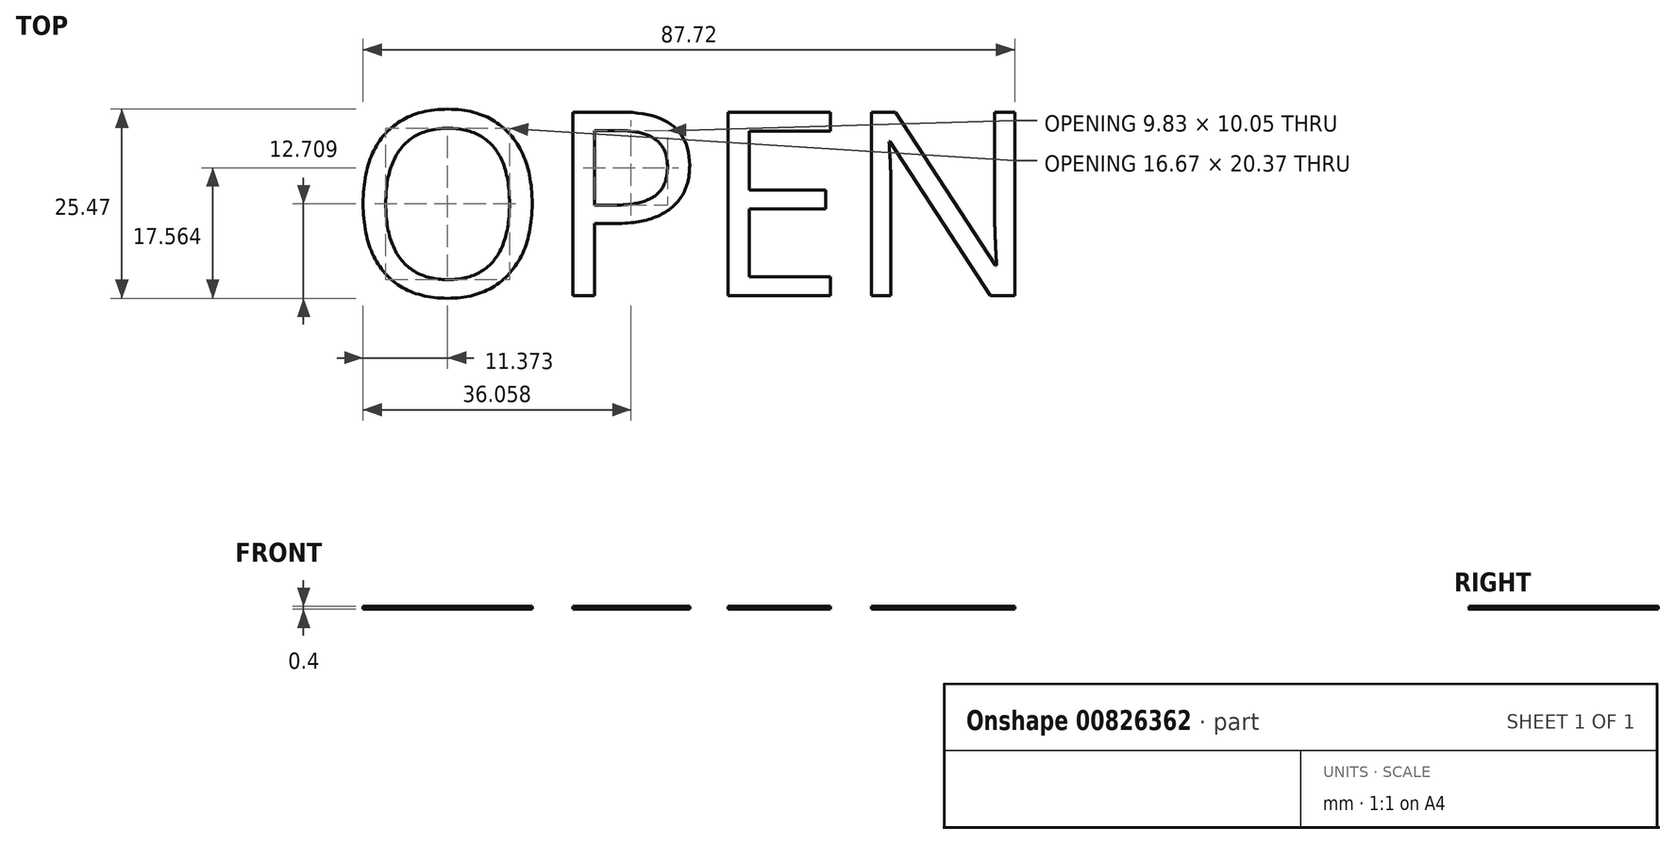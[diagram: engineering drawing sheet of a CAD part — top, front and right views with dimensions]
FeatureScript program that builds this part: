
annotation { "Feature Type Name" : "Feature", "Feature Type Description" : "" }
export const myFeature = defineFeature(function(context is Context, id is Id, definition is map)
    precondition{}
    {
        {
            var Q0;
            Q0=qCreatedBy(makeId("Top.planeOp"),FACE);
            var sketch = newSketch(context, id + "F0", { "sketchPlane" : qUnion([Q0])});
            skText(sketch, "E0", { "text": "OPEN", "fontName": "OpenSans-Regular.ttf"});
            skPoint(sketch, "E1.visualSharp", {"position": v(-49.43, 16.69) * mm});
            skPoint(sketch, "E2.visualSharp", {"position": v(-49.43, -16.69) * mm});
            skPoint(sketch, "E3.visualSharp", {"position": v(49.43, -16.69) * mm});
            const initialGuessF0  = {"E0": [-0.046, -0.01232, 1, 0, 0.02495]};
            skSetInitialGuess(sketch, initialGuessF0);
            skSolve(sketch);
        }
        {
            var Q0;
            Q0 = qSketchRegion(id + "F0", true);
            extrude(context, id + "F1", {"entities" : qUnion([Q0]), "depth" : 0.4 * mm, "offsetDistance" : 25 * mm});
        }
    });
